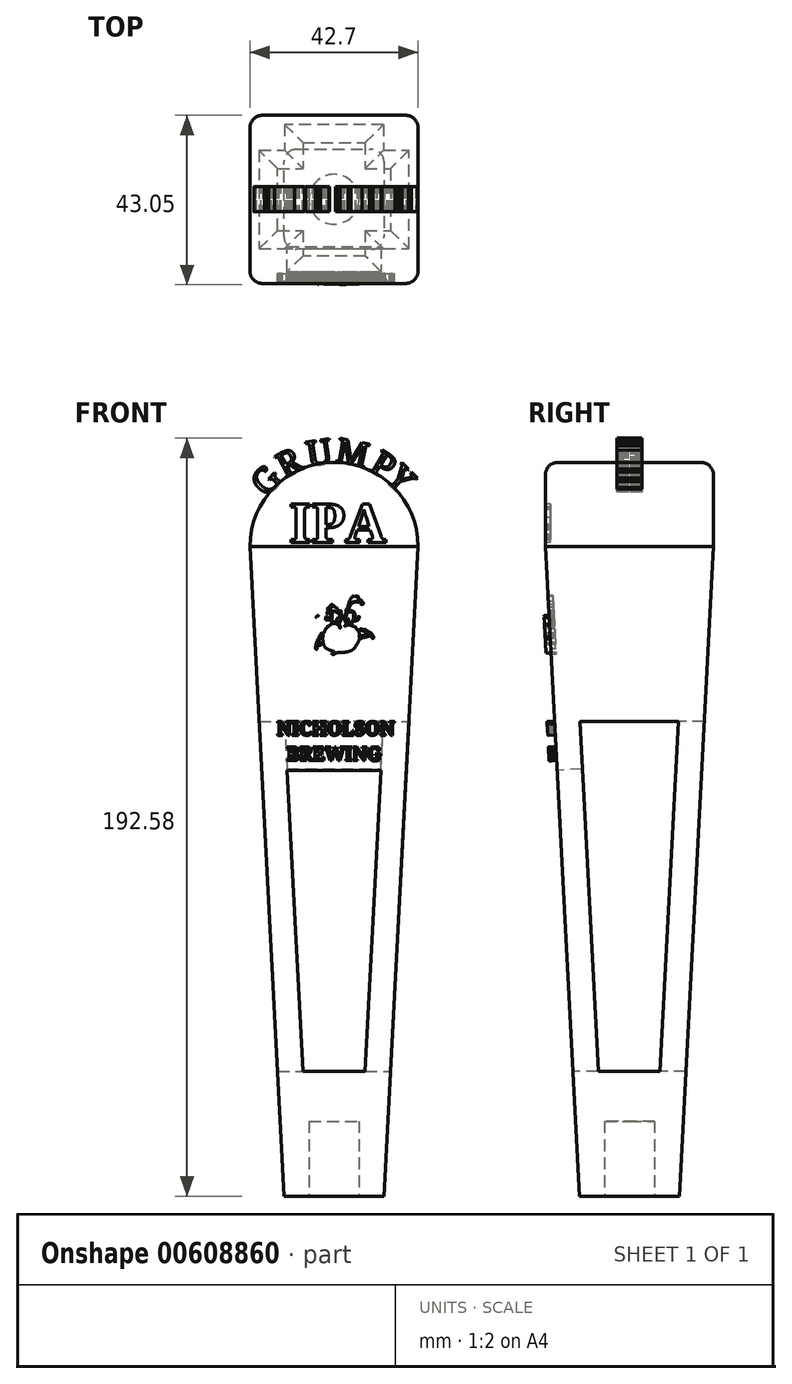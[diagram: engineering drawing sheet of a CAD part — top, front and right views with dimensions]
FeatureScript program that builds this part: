
annotation { "Feature Type Name" : "Feature", "Feature Type Description" : "" }
export const myFeature = defineFeature(function(context is Context, id is Id, definition is map)
    precondition{}
    {
        {
            var Q0;
            Q0=qCreatedBy(makeId("Top.planeOp"),FACE);
            var sketch = newSketch(context, id + "F0", { "sketchPlane" : qUnion([Q0])});
            skLineSegment(sketch, "E0.bottom", {"start": v(12.7, -12.7) * mm, "end": v(-12.7, -12.7) * mm});
            skLineSegment(sketch, "E0.top", {"start": v(12.7, 12.7) * mm, "end": v(-12.7, 12.7) * mm});
            skLineSegment(sketch, "E0.left", {"start": v(12.7, -12.7) * mm, "end": v(12.7, 12.7) * mm});
            skLineSegment(sketch, "E0.right", {"start": v(-12.7, -12.7) * mm, "end": v(-12.7, 12.7) * mm});
            skPoint(sketch, "E0.middle", {"position": v(0, 0) * mm});
            skSolve(sketch);
        }
        {
            var Q0;
            Q0=makeQuery(id+"F0.imprint","IMPRINT",FACE,{"disambiguationData":[TD([[makeQuery(id+"F0.imprint","IMPRINT",EDGE,{"derivedFrom":sQuery(id+"F0.wireOp",EDGE,"E0.bottom")}),-1.0]])]});
            extrude(context, id + "F1", {"entities" : qUnion([Q0]), "depth" : 165.1 * mm, "offsetDistance" : 25.4 * mm, "hasDraft" : true, "draftAngle" : 3 * degree});
        }
        {
            var Q0;
            Q0=qCreatedBy(makeId("Front.planeOp"),FACE);
            var sketch = newSketch(context, id + "F2", { "sketchPlane" : qUnion([Q0])});
            skArc(sketch, "E1", {"start": v(21.35, 165.1) * mm, "mid": v(0, 186.45) * mm, "end": v(-21.35, 165.1) * mm});
            skLineSegment(sketch, "E2", {"start": v(0, 165.1) * mm, "end": v(-21.35, 165.1) * mm});
            skLineSegment(sketch, "E3", {"start": v(-21.35, 165.1) * mm, "end": v(21.35, 165.1) * mm});
            skSolve(sketch);
        }
        {
            var Q0;
            Q0=makeQuery(id+"F1.opExtrude","SWEPT_FACE",FACE,{"disambiguationData":[OSD([sQuery(id+"F0.wireOp",EDGE,"E0.bottom")])]});
            var sketch = newSketch(context, id + "F3", { "sketchPlane" : qUnion([Q0])});
            skFitSpline(sketch, "E4", {"points": [v(-3.93, 148.41) * mm, v(-6, 146.06) * mm, v(-7.77, 144.13) * mm, v(-9.42, 142.29) * mm, v(-9.9, 141.3) * mm, v(-10.32, 140.28) * mm, v(-10.2, 139.42) * mm, v(-10.01, 139.18) * mm, v(-9.58, 140.32) * mm, v(-9.19, 140.67) * mm, v(-9.5, 139.54) * mm, v(-9.58, 138.12) * mm, v(-8.52, 135.3) * mm, v(-7.62, 134.55) * mm, v(-7.5, 135.65) * mm, v(-7.26, 135.68) * mm, v(-7.1, 134.94) * mm, v(-7.19, 133.52) * mm, v(-6.24, 131.8) * mm, v(-4.71, 129.75) * mm, v(-4, 129.4) * mm, v(-4.09, 130.18) * mm, v(-4.09, 131.05) * mm, v(-3.81, 131.24) * mm, v(-3.7, 129.48) * mm, v(-2.9, 128.02) * mm, v(-0.9, 126.3) * mm, v(-0.67, 126.92) * mm, v(0.94, 129.4) * mm, v(3.88, 130.9) * mm, v(6.4, 131.95) * mm, v(7.14, 132.7) * mm, v(7.72, 134.3) * mm, v(8.04, 134.3) * mm, v(8, 133.56) * mm, v(7.69, 132.82) * mm, v(9.3, 133.84) * mm, v(10, 135.02) * mm, v(10.27, 134.9) * mm, v(10.08, 134.03) * mm, v(11.1, 135.37) * mm, v(11.9, 136.77) * mm, v(12.52, 139.46) * mm, v(12.12, 141.58) * mm, v(12.47, 142.22) * mm, v(11.73, 144.3) * mm, v(10.14, 145.79) * mm, v(8.81, 147.12) * mm, v(8.9, 146.18) * mm, v(9.8, 145.34) * mm, v(11.23, 143.21) * mm, v(11.38, 141.78) * mm, v(10.2, 140.59) * mm, v(8.27, 140.14) * mm, v(6.59, 140) * mm, v(5.8, 139.7) * mm, v(6.49, 140.39) * mm, v(5.84, 140.2) * mm, v(4.95, 138.95) * mm, v(3.52, 137.72) * mm, v(1.54, 136.97) * mm, v(-0.63, 137.37) * mm, v(-1.52, 137.96) * mm, v(-2.07, 138.8) * mm, v(-2.16, 139.6) * mm, v(-2.36, 138.8) * mm, v(-3.45, 138.66) * mm, v(-4.34, 138.7) * mm, v(-5.82, 139.35) * mm, v(-6.67, 140.56) * mm, v(-6.75, 142.27) * mm, v(-6.1, 143.76) * mm, v(-5.13, 145.13) * mm, v(-4.32, 146.04) * mm, v(-3.35, 146.65) * mm, v(-3.64, 146.83) * mm, v(-3.84, 146.83) * mm, v(-3.93, 148.41) * mm]});
            skFitSpline(sketch, "E5", {"points": [v(-3.93, 148.41) * mm, v(-3.27, 149.51) * mm, v(-2.97, 151.48) * mm, v(-2.12, 153.44) * mm, v(-0.83, 155.33) * mm, v(1.17, 156.56) * mm, v(3.21, 156.93) * mm, v(5.58, 155.85) * mm, v(7.25, 154.11) * mm, v(8.1, 152.3) * mm, v(8.58, 148.07) * mm, v(9.33, 147.12) * mm, v(9.72, 147.12) * mm, v(9.74, 148) * mm, v(9.69, 149.97) * mm, v(9.35, 152.98) * mm, v(8.03, 155.62) * mm, v(6.08, 157.5) * mm, v(3.87, 158.7) * mm, v(1.8, 158.96) * mm, v(0, 158.5) * mm, v(-2.07, 156.81) * mm, v(-2.76, 155.16) * mm, v(-3.62, 153.34) * mm, v(-3.65, 154.07) * mm, v(-3.12, 155.3) * mm, v(-2.6, 156.78) * mm, v(-1.64, 157.9) * mm, v(-2.9, 157.37) * mm, v(-4.3, 155.92) * mm, v(-4.94, 154.73) * mm, v(-5.46, 152.82) * mm, v(-5.7, 151.63) * mm, v(-5.96, 151.46) * mm, v(-5.96, 151.96) * mm, v(-5.56, 153.74) * mm, v(-6.16, 152.82) * mm, v(-7.6, 151.76) * mm, v(-9.06, 150.83) * mm, v(-10.94, 149.78) * mm, v(-11.73, 148.92) * mm, v(-12.23, 147.66) * mm, v(-12.26, 146.37) * mm, v(-11.8, 145.41) * mm, v(-10.74, 144.72) * mm, v(-9.62, 144.13) * mm, v(-8.53, 144) * mm, v(-7.77, 144.13) * mm, v(-6, 146.06) * mm, v(-6, 146.9) * mm, v(-6, 147.81) * mm, v(-5.51, 147.85) * mm, v(-5.5, 147.12) * mm, v(-5.34, 146.98) * mm, v(-5.24, 147.12) * mm, v(-4.72, 147.8) * mm, v(-4.12, 148.41) * mm, v(-3.93, 148.41) * mm]});
            skFitSpline(sketch, "E6", {"points": [v(9.26, 143.2) * mm, v(9.68, 142.71) * mm, v(9.84, 142.49) * mm, v(10.1, 142.68) * mm, v(10.17, 142.96) * mm, v(9.79, 143.38) * mm, v(9.47, 143.89) * mm, v(8.6, 144.45) * mm, v(7.83, 144.85) * mm, v(7.03, 144.92) * mm, v(6.6, 144.97) * mm, v(6.57, 144.74) * mm, v(7.05, 144.59) * mm, v(8.06, 144.13) * mm, v(8.81, 143.76) * mm, v(8.23, 143.66) * mm, v(7.36, 143.33) * mm, v(6.63, 143.12) * mm, v(6.43, 143.05) * mm, v(6.42, 143.87) * mm, v(6.03, 144.7) * mm, v(5.37, 145.48) * mm, v(4.53, 145.88) * mm, v(4.04, 146.06) * mm, v(3.36, 146.06) * mm, v(2.78, 145.8) * mm, v(2.7, 145.9) * mm, v(3, 146.06) * mm, v(3.15, 146.34) * mm, v(2.85, 146.9) * mm, v(2.73, 147.39) * mm, v(2.7, 147.74) * mm, v(2.33, 147.9) * mm, v(1.9, 147.93) * mm, v(1.82, 147.7) * mm, v(1.84, 147.28) * mm, v(1.68, 147.12) * mm, v(1.43, 146.56) * mm, v(1.43, 146.06) * mm, v(1.63, 145.62) * mm, v(1.63, 145.32) * mm, v(1.47, 145.27) * mm, v(1.36, 145.67) * mm, v(0.98, 146.06) * mm, v(0.5, 146.4) * mm, v(-0.33, 146.39) * mm, v(-1.01, 146.06) * mm, v(-1.92, 145.27) * mm, v(-2.31, 144.6) * mm, v(-2.5, 144.13) * mm, v(-3.04, 143.99) * mm, v(-3.57, 143.42) * mm, v(-4.15, 142.16) * mm, v(-4.6, 140.89) * mm, v(-4.72, 140.12) * mm, v(-4.66, 139.86) * mm, v(-4.31, 139.86) * mm, v(-4.3, 140.34) * mm, v(-4.17, 140.65) * mm, v(-3.55, 140.85) * mm, v(-2.7, 141.16) * mm, v(-2.43, 140.57) * mm, v(-1.88, 140.06) * mm, v(-0.98, 139.6) * mm, v(0, 139.27) * mm, v(0, 139.02) * mm, v(-0.4, 138.86) * mm, v(-0.5, 138.57) * mm, v(0, 138.49) * mm, v(0.36, 138.88) * mm, v(0.79, 139) * mm, v(1.61, 139.02) * mm, v(2.54, 139.08) * mm, v(3.34, 139.22) * mm, v(4.54, 139.67) * mm, v(5.4, 140.36) * mm, v(5.89, 141.28) * mm, v(6.26, 141.79) * mm, v(6.36, 142.18) * mm, v(6.48, 142.44) * mm, v(7.83, 142.85) * mm, v(8.81, 143.14) * mm, v(9.26, 143.2) * mm]});
            skFitSpline(sketch, "E7", {"points": [v(-2.9, 143.68) * mm, v(-3.3, 143.15) * mm, v(-3.66, 142.3) * mm, v(-3.93, 141.14) * mm, v(-3.58, 141.3) * mm, v(-2.77, 141.57) * mm, v(-2.77, 141.82) * mm, v(-2.87, 142.47) * mm, v(-2.9, 143.68) * mm]});
            skFitSpline(sketch, "E8", {"points": [v(4.12, 146.35) * mm, v(3.75, 146.31) * mm, v(3.45, 146.42) * mm, v(3.5, 146.56) * mm, v(3.71, 146.98) * mm, v(3.68, 147.44) * mm, v(3.55, 147.7) * mm, v(3.08, 147.7) * mm, v(2.93, 147.93) * mm, v(3.16, 148.41) * mm, v(3.3, 148.96) * mm, v(3.82, 149.22) * mm, v(4.53, 149.28) * mm, v(4.88, 148.93) * mm, v(4.97, 148.41) * mm, v(4.9, 147.7) * mm, v(4.73, 147.12) * mm, v(4.12, 146.35) * mm]});
            skFitSpline(sketch, "E9", {"points": [v(0.95, 146.85) * mm, v(0.73, 147.12) * mm, v(0.75, 147.54) * mm, v(1.08, 147.9) * mm, v(1.6, 148.1) * mm, v(1.43, 148.6) * mm, v(0.82, 149.11) * mm, v(0.42, 149.4) * mm, v(0, 149.52) * mm, v(-0.36, 149.28) * mm, v(-0.47, 148.74) * mm, v(-0.53, 148.1) * mm, v(-0.55, 147.54) * mm, v(-0.4, 147.12) * mm, v(0, 146.72) * mm, v(0.48, 146.78) * mm, v(0.95, 146.85) * mm]});
            skFitSpline(sketch, "E10", {"points": [v(3.53, 149.67) * mm, v(3.91, 150.38) * mm, v(4.1, 151.02) * mm, v(4.46, 151.46) * mm, v(5.1, 151.83) * mm, v(5.73, 151.88) * mm, v(6.25, 151.88) * mm, v(6.6, 151.7) * mm, v(6.8, 151.32) * mm, v(7.16, 151.14) * mm, v(7.44, 151.46) * mm, v(7.18, 152) * mm, v(6.73, 152.4) * mm, v(6.47, 152.58) * mm, v(6.1, 152.67) * mm, v(6.09, 152.82) * mm, v(6.2, 153.1) * mm, v(6.12, 153.29) * mm, v(5.51, 153.35) * mm, v(5.22, 153.15) * mm, v(5.05, 153.27) * mm, v(4.85, 153.42) * mm, v(4.62, 153.24) * mm, v(4.01, 152.15) * mm, v(3.7, 151.3) * mm, v(3.48, 150.56) * mm, v(3.37, 150.15) * mm, v(3.05, 149.88) * mm, v(3.04, 149.24) * mm, v(2.84, 148.6) * mm, v(2.6, 148.23) * mm, v(2.1, 148.3) * mm, v(1.9, 148.73) * mm, v(1.82, 149.24) * mm, v(1.82, 149.55) * mm, v(1.43, 149.52) * mm, v(1.19, 149.47) * mm, v(0.98, 149.85) * mm, v(0.65, 150.35) * mm, v(0.23, 150.64) * mm, v(-0.21, 151.06) * mm, v(-0.67, 151.19) * mm, v(-0.87, 151.06) * mm, v(-0.7, 150.77) * mm, v(-0.46, 150.53) * mm, v(-0.8, 150.46) * mm, v(-1.25, 150.58) * mm, v(-1.55, 150.26) * mm, v(-1.78, 150.05) * mm, v(-1.28, 149.93) * mm, v(-1.1, 149.9) * mm, v(-1.73, 149.3) * mm, v(-1.8, 148.94) * mm, v(-1.65, 148.84) * mm, v(-1.33, 149.12) * mm, v(-0.92, 149.52) * mm, v(-0.7, 149.57) * mm, v(-0.6, 149.29) * mm, v(-0.84, 148.9) * mm, v(-0.87, 148.41) * mm, v(-0.79, 147.93) * mm, v(-0.77, 147.7) * mm, v(-0.8, 147.52) * mm, v(-0.96, 147.4) * mm, v(-1.27, 147.6) * mm, v(-1.62, 147.9) * mm, v(-1.75, 148.02) * mm, v(-1.95, 148.12) * mm, v(-2.1, 147.93) * mm, v(-2.1, 147.5) * mm, v(-2.1, 147.32) * mm, v(-1.47, 147.26) * mm, v(-0.92, 147.12) * mm, v(-0.51, 146.8) * mm, v(-0.33, 146.39) * mm, v(-0.18, 146.42) * mm, v(0.2, 146.45) * mm, v(0.5, 146.4) * mm, v(0.98, 146.06) * mm, v(1.36, 145.67) * mm, v(1.47, 145.27) * mm, v(1.63, 145.32) * mm, v(1.63, 145.62) * mm, v(1.43, 146.06) * mm, v(1.43, 146.56) * mm, v(1.68, 147.12) * mm, v(1.84, 147.28) * mm, v(1.82, 147.7) * mm, v(1.9, 147.93) * mm, v(2.33, 147.9) * mm, v(2.7, 147.74) * mm, v(2.73, 147.39) * mm, v(2.85, 146.9) * mm, v(3.15, 146.34) * mm, v(3, 146.06) * mm, v(2.7, 145.9) * mm, v(2.78, 145.8) * mm, v(3.36, 146.06) * mm, v(4.04, 146.06) * mm, v(4.3, 145.97) * mm, v(4.35, 146.06) * mm, v(4.35, 146.34) * mm, v(4.62, 146.56) * mm, v(4.9, 146.84) * mm, v(5.37, 147.03) * mm, v(5.8, 147.12) * mm, v(6.18, 147.33) * mm, v(6.27, 147.54) * mm, v(6.34, 147.7) * mm, v(6.53, 147.93) * mm, v(6.36, 148.13) * mm, v(6.02, 148.04) * mm, v(5.79, 147.7) * mm, v(5.67, 147.7) * mm, v(5.43, 147.42) * mm, v(5.1, 147.12) * mm, v(5.1, 147.4) * mm, v(5.26, 148.3) * mm, v(5.3, 148.7) * mm, v(5.23, 149.08) * mm, v(5, 149.42) * mm, v(4.42, 149.64) * mm, v(3.96, 149.58) * mm, v(3.6, 149.47) * mm, v(3.52, 149.53) * mm, v(3.53, 149.67) * mm]});
            skLineSegment(sketch, "E11", {"start": v(-2.9, 143.68) * mm, "end": v(-3.04, 143.99) * mm});
            skLineSegment(sketch, "E12", {"start": v(-2.9, 143.68) * mm, "end": v(-2.5, 144.13) * mm});
            skLineSegment(sketch, "E13", {"start": v(-2.77, 141.57) * mm, "end": v(-2.7, 141.16) * mm});
            skLineSegment(sketch, "E14", {"start": v(0, 139.02) * mm, "end": v(0.36, 138.88) * mm});
            skLineSegment(sketch, "E15", {"start": v(6.48, 142.44) * mm, "end": v(6.43, 143.05) * mm});
            skSolve(sketch);
        }
        {
            var Q0;
            {var subQ0=sQuery(id+"F3.wireOp",EDGE,"E11");Q0=makeQuery(id+"F3.imprint","IMPRINT",FACE,{"disambiguationData":[TD([[makeQuery(id+"F3.imprint","IMPRINT",EDGE,{"derivedFrom":subQ0}),1.0]])]});}
            var Q1;
            {var subQ0=sQuery(id+"F3.wireOp",EDGE,"E14");Q1=makeQuery(id+"F3.imprint","IMPRINT",FACE,{"disambiguationData":[TD([[makeQuery(id+"F3.imprint","IMPRINT",EDGE,{"derivedFrom":subQ0}),-1.0]])]});}
            var Q2;
            {var subQ0=sQuery(id+"F3.wireOp",EDGE,"E15");Q2=makeQuery(id+"F3.imprint","IMPRINT",FACE,{"disambiguationData":[TD([[makeQuery(id+"F3.imprint","IMPRINT",EDGE,{"derivedFrom":subQ0}),-1.0]])]});}
            var Q3;
            Q3=makeQuery(id+"F3.imprint","IMPRINT",FACE,{"disambiguationData":[TD([[makeQuery(id+"F3.imprint","IMPRINT",EDGE,{"derivedFrom":sQuery(id+"F3.wireOp",EDGE,"E8")}),1.0]])]});
            extrude(context, id + "F4", {"entities" : qUnion([Q0, Q1, Q2, Q3]), "operationType" : NewBodyOperationType.REMOVE, "oppositeDirection" : true, "depth" : 1.27 * mm, "offsetDistance" : 25.4 * mm});
        }
        {
            var Q0;
            {var subQ0=sQuery(id+"F3.wireOp",EDGE,"E5");var subQ1=sQuery(id+"F3.wireOp",EDGE,"E4");var subQ7=makeQuery(id+"F3.imprint","INTERSECT",VERTEX,{"disambiguationData":[OD(2.0)],"derivedFrom":[subQ1,subQ0]});Q0=makeQuery(id+"F3.imprint","IMPRINT",FACE,{"disambiguationData":[TD([[makeQuery(id+"F3.imprint","IMPRINT",EDGE,{"disambiguationData":[TD([[subQ7,1.0]])],"derivedFrom":subQ1}),-1.0]])]});}
            extrude(context, id + "F5", {"entities" : qUnion([Q0]), "operationType" : NewBodyOperationType.REMOVE, "oppositeDirection" : true, "depth" : 1.27 * mm, "offsetDistance" : 25.4 * mm});
        }
        {
            var Q0;
            {var subQ0=sQuery(id+"F3.wireOp",EDGE,"E5");var subQ1=sQuery(id+"F3.wireOp",EDGE,"E4");var subQ8=makeQuery(id+"F3.imprint","INTERSECT",VERTEX,{"disambiguationData":[OD(0.0)],"derivedFrom":[subQ1,subQ0]});Q0=makeQuery(id+"F3.imprint","IMPRINT",FACE,{"disambiguationData":[TD([[makeQuery(id+"F3.imprint","IMPRINT",EDGE,{"disambiguationData":[TD([[subQ8,1.0]])],"derivedFrom":subQ1}),1.0]])]});}
            var Q1;
            {var subQ9=sQuery(id+"F3.wireOp",EDGE,"E12");Q1=makeQuery(id+"F3.imprint","IMPRINT",FACE,{"disambiguationData":[TD([[makeQuery(id+"F3.imprint","IMPRINT",EDGE,{"derivedFrom":subQ9}),-1.0]])]});}
            extrude(context, id + "F6", {"entities" : qUnion([Q0, Q1]), "operationType" : NewBodyOperationType.ADD, "depth" : 1.27 * mm, "offsetDistance" : 25.4 * mm});
        }
        {
            var Q0;
            Q0=makeQuery(id+"F1.opExtrude","CAP_FACE",FACE,{"disambiguationData":[OSD([sQuery(id+"F0.wireOp",EDGE,"E0.bottom"),sQuery(id+"F0.wireOp",EDGE,"E0.top"),sQuery(id+"F0.wireOp",EDGE,"E0.left"),sQuery(id+"F0.wireOp",EDGE,"E0.right")])],"isStart":false});
            var sketch = newSketch(context, id + "F7", { "sketchPlane" : qUnion([Q0])});
            skLineSegment(sketch, "E16.bottom", {"start": v(-21.35, 21.35) * mm, "end": v(21.35, 21.35) * mm});
            skLineSegment(sketch, "E16.top", {"start": v(-21.35, -21.35) * mm, "end": v(21.35, -21.35) * mm});
            skLineSegment(sketch, "E16.left", {"start": v(-21.35, 21.35) * mm, "end": v(-21.35, -21.35) * mm});
            skLineSegment(sketch, "E16.right", {"start": v(21.35, 21.35) * mm, "end": v(21.35, -21.35) * mm});
            skSolve(sketch);
        }
        {
            var Q0;
            {var subQ0=sQuery(id+"F2.wireOp",EDGE,"E1");Q0=makeQuery(id+"F2.imprint","IMPRINT",FACE,{"disambiguationData":[TD([[makeQuery(id+"F2.imprint","IMPRINT",EDGE,{"derivedFrom":subQ0}),1.0]])]});}
            extrude(context, id + "F8", {"entities" : qUnion([Q0]), "operationType" : NewBodyOperationType.ADD, "depth" : 21.35 * mm, "offsetDistance" : 25.4 * mm, "hasSecondDirection" : true, "secondDirectionOppositeDirection" : true, "secondDirectionDepth" : 21.35 * mm});
        }
        {
            var Q0;
            Q0=qCreatedBy(makeId("Front.planeOp"),FACE);
            var sketch = newSketch(context, id + "F9", { "sketchPlane" : qUnion([Q0])});
            skLineSegment(sketch, "E17", {"start": v(0, 0) * mm, "end": v(0, 31.75) * mm, "construction": true});
            skLineSegment(sketch, "E18", {"start": v(0, 31.75) * mm, "end": v(-7.91, 31.75) * mm});
            skLineSegment(sketch, "E19", {"start": v(-7.91, 31.75) * mm, "end": v(-12.57, 120.65) * mm});
            skLineSegment(sketch, "E20", {"start": v(-12.57, 120.65) * mm, "end": v(12.57, 120.65) * mm});
            skLineSegment(sketch, "E21", {"start": v(12.57, 120.65) * mm, "end": v(7.91, 31.75) * mm});
            skLineSegment(sketch, "E22", {"start": v(7.91, 31.75) * mm, "end": v(0, 31.75) * mm});
            skLineSegment(sketch, "E23", {"start": v(0, 31.75) * mm, "end": v(0, 31.75) * mm});
            skSolve(sketch);
        }
        {
            var Q0;
            Q0 = qSketchRegion(id + "F9", true);
            extrude(context, id + "F10", {"entities" : qUnion([Q0]), "operationType" : NewBodyOperationType.REMOVE, "oppositeDirection" : true, "depth" : 25.4 * mm, "offsetDistance" : 25.4 * mm, "hasSecondDirection" : true, "secondDirectionOppositeDirection" : false, "secondDirectionDepth" : 25.4 * mm});
        }
        {
            var Q0;
            Q0=qCreatedBy(makeId("Right.planeOp"),FACE);
            var sketch = newSketch(context, id + "F11", { "sketchPlane" : qUnion([Q0])});
            skLineSegment(sketch, "E24", {"start": v(0, 0) * mm, "end": v(0, 31.75) * mm, "construction": true});
            skLineSegment(sketch, "E25", {"start": v(0, 31.75) * mm, "end": v(-7.91, 31.75) * mm});
            skLineSegment(sketch, "E26", {"start": v(-7.91, 31.75) * mm, "end": v(-12.57, 120.65) * mm});
            skLineSegment(sketch, "E27", {"start": v(-12.57, 120.65) * mm, "end": v(12.44, 120.65) * mm});
            skLineSegment(sketch, "E28", {"start": v(12.44, 120.65) * mm, "end": v(7.78, 31.75) * mm});
            skLineSegment(sketch, "E29", {"start": v(7.78, 31.75) * mm, "end": v(0, 31.75) * mm});
            skSolve(sketch);
        }
        {
            var Q0;
            Q0 = qSketchRegion(id + "F11", true);
            extrude(context, id + "F12", {"entities" : qUnion([Q0]), "operationType" : NewBodyOperationType.REMOVE, "oppositeDirection" : true, "depth" : 25.4 * mm, "offsetDistance" : 25.4 * mm, "hasSecondDirection" : true, "secondDirectionOppositeDirection" : false, "secondDirectionDepth" : 25.4 * mm});
        }
        {
            var Q0;
            Q0=makeQuery(id+"F8.opExtrude","CAP_FACE",FACE,{"disambiguationData":[OSD([sQuery(id+"F2.wireOp",EDGE,"E1"),sQuery(id+"F2.wireOp",EDGE,"E3")])],"isStart":false});
            var sketch = newSketch(context, id + "F13", { "sketchPlane" : qUnion([Q0])});
            skText(sketch, "E30", { "text": "IPA", "fontName": "NotoSerif-Bold.ttf"});
            const initialGuessF13  = {"E30": [-0.01126, 0.1661, 1, 0, 0.00982]};
            skSetInitialGuess(sketch, initialGuessF13);
            skSolve(sketch);
        }
        {
            var Q0;
            Q0 = qSketchRegion(id + "F13", true);
            extrude(context, id + "F14", {"entities" : qUnion([Q0]), "operationType" : NewBodyOperationType.REMOVE, "oppositeDirection" : true, "depth" : 1.27 * mm, "offsetDistance" : 25.4 * mm});
        }
        {
            var Q0;
            Q0=qCreatedBy(makeId("Front.planeOp"),FACE);
            var sketch = newSketch(context, id + "F15", { "sketchPlane" : qUnion([Q0])});
            skText(sketch, "E31", { "text": "G", "fontName": "NotoSerif-Regular.ttf"});
            skLineSegment(sketch, "E32", {"start": v(0, 165.1) * mm, "end": v(-14.95, 179.79) * mm, "construction": true});
            skLineSegment(sketch, "E33", {"start": v(0, 165.1) * mm, "end": v(-9.68, 183.69) * mm, "construction": true});
            skText(sketch, "E34", { "text": "R", "fontName": "NotoSerif-Regular.ttf"});
            skText(sketch, "E35", { "text": "U", "fontName": "NotoSerif-Regular.ttf"});
            skLineSegment(sketch, "E36", {"start": v(0, 165.1) * mm, "end": v(-3.1, 185.82) * mm, "construction": true});
            skText(sketch, "E37", { "text": "M", "fontName": "NotoSerif-Regular.ttf"});
            skLineSegment(sketch, "E38", {"start": v(0, 165.1) * mm, "end": v(4.18, 185.63) * mm, "construction": true});
            skText(sketch, "E39", { "text": "P", "fontName": "NotoSerif-Regular.ttf"});
            skLineSegment(sketch, "E40", {"start": v(0, 165.1) * mm, "end": v(10.95, 182.97) * mm, "construction": true});
            skText(sketch, "E41", { "text": "Y", "fontName": "NotoSerif-Regular.ttf"});
            skLineSegment(sketch, "E42", {"start": v(0, 165.1) * mm, "end": v(14.95, 179.79) * mm, "construction": true});
            const initialGuessF15  = {"E31": [-0.0173, 0.1774, 0.7009, 0.71325, 0.00635], "E34": [-0.01252, 0.1822, 0.88701, 0.46175, 0.00635], "E35": [-0.00644, 0.18532, 0.98902, 0.1478, 0.00635], "E37": [0, 0.18648, 0.97992, -0.19937, 0.00635], "E39": [0.00858, 0.18442, 0.85264, -0.5225, 0.00635], "E41": [0.01279, 0.18198, 0.7009, -0.71325, 0.00635]};
            skSetInitialGuess(sketch, initialGuessF15);
            skSolve(sketch);
        }
        {
            var Q0;
            Q0 = qSketchRegion(id + "F15", true);
            extrude(context, id + "F16", {"entities" : qUnion([Q0]), "depth" : 3.17 * mm, "offsetDistance" : 25.4 * mm, "hasSecondDirection" : true, "secondDirectionOppositeDirection" : true, "secondDirectionDepth" : 3.17 * mm});
        }
        {
            var Q0;
            {var subQ0=sQuery(id+"F3.wireOp",EDGE,"E15");var subQ1=sQuery(id+"F3.wireOp",EDGE,"E6");var subQ2=makeQuery(id+"F3.imprint","INTERSECT",VERTEX,{"disambiguationData":[OD(0.0)],"derivedFrom":[subQ1,subQ0]});var subQ3=sQuery(id+"F3.wireOp",EDGE,"E10");var subQ4=makeQuery(id+"F3.imprint","INTERSECT",VERTEX,{"disambiguationData":[OD(0.0)],"derivedFrom":[subQ1,subQ3]});var subQ5=sQuery(id+"F3.wireOp",EDGE,"E5");var subQ6=sQuery(id+"F3.wireOp",EDGE,"E4");var subQ7=makeQuery(id+"F3.imprint","INTERSECT",VERTEX,{"disambiguationData":[OD(2.0)],"derivedFrom":[subQ6,subQ5]});var subQ8=makeQuery(id+"F3.imprint","INTERSECT",VERTEX,{"disambiguationData":[OD(3.0)],"derivedFrom":[subQ6,subQ5]});var subQ9=sQuery(id+"F0.wireOp",EDGE,"E0.right");var subQ10=makeQuery(id+"F1.opExtrude","SWEPT_FACE",FACE,{"disambiguationData":[OSD([subQ9])]});var subQ11=makeQuery(id+"F3.imprint","INTERSECT",VERTEX,{"disambiguationData":[OD(6.0)],"derivedFrom":[subQ6,subQ5]});var subQ13=sQuery(id+"F0.wireOp",EDGE,"E0.left");var subQ14=sQuery(id+"F0.wireOp",EDGE,"E0.top");var subQ15=sQuery(id+"F0.wireOp",EDGE,"E0.bottom");var subQ16=makeQuery(id+"F1.opExtrude","CAP_FACE",FACE,{"disambiguationData":[OSD([subQ15,subQ14,subQ13,subQ9])],"isStart":false});var subQ17=sQuery(id+"F3.wireOp",EDGE,"E14");var subQ18=makeQuery(id+"F3.imprint","INTERSECT",VERTEX,{"disambiguationData":[OD(0.0)],"derivedFrom":[subQ1,subQ17]});var subQ19=makeQuery(id+"F3.imprint","INTERSECT",VERTEX,{"disambiguationData":[OD(1.0)],"derivedFrom":[subQ1,subQ17]});var subQ20=makeQuery(id+"F4.opExtrude","SWEPT_FACE",FACE,{"disambiguationData":[OSD([subQ1]),TDD([makeQuery(id+"F3.imprint","IMPRINT",EDGE,{"disambiguationData":[TD([[subQ18,-1.0]])],"derivedFrom":subQ1})])]});var subQ21=sQuery(id+"F3.wireOp",EDGE,"E13");var subQ22=makeQuery(id+"F4.opExtrude","SWEPT_FACE",FACE,{"disambiguationData":[OSD([subQ0])]});var subQ23=makeQuery(id+"F4.opExtrude","SWEPT_FACE",FACE,{"disambiguationData":[OSD([subQ17])]});var subQ24=makeQuery(id+"F4.opExtrude","SWEPT_FACE",FACE,{"disambiguationData":[OSD([subQ21])]});var subQ25=sQuery(id+"F3.wireOp",EDGE,"E11");var subQ26=makeQuery(id+"F4.opExtrude","SWEPT_FACE",FACE,{"disambiguationData":[OSD([subQ25])]});var subQ29=makeQuery(id+"F4.opExtrude","SWEPT_FACE",FACE,{"disambiguationData":[OSD([subQ3]),TDD([makeQuery(id+"F3.imprint","IMPRINT",EDGE,{"disambiguationData":[TD([[subQ4,1.0]])],"derivedFrom":subQ3}),makeQuery(id+"F3.imprint","IMPRINT",EDGE,{"disambiguationData":[TD([[subQ4,-1.0]])],"derivedFrom":subQ3})])]});var subQ30=makeQuery(id+"F1.opExtrude","SWEPT_FACE",FACE,{"disambiguationData":[OSD([subQ13])]});var subQ31=makeQuery(id+"F1.opExtrude","CAP_FACE",FACE,{"disambiguationData":[OSD([subQ15,subQ14,subQ13,subQ9])],"isStart":true});var subQ32=makeQuery(id+"F3.imprint","INTERSECT",VERTEX,{"derivedFrom":[subQ1,subQ21]});var subQ33=makeQuery(id+"F4.opExtrude","SWEPT_FACE",FACE,{"disambiguationData":[OSD([subQ1]),TDD([makeQuery(id+"F3.imprint","IMPRINT",EDGE,{"disambiguationData":[TD([[makeQuery(id+"F3.imprint","INTERSECT",VERTEX,{"derivedFrom":[subQ1,subQ25]}),-1.0]])],"derivedFrom":subQ1})])]});var subQ34=sQuery(id+"F3.wireOp",EDGE,"E12");var subQ35=makeQuery(id+"F1.opExtrude","SWEPT_FACE",FACE,{"disambiguationData":[OSD([subQ15])]});var subQ36=makeQuery(id+"F3.imprint","INTERSECT",VERTEX,{"disambiguationData":[OD(7.0)],"derivedFrom":[subQ1,subQ3]});var subQ37=makeQuery(id+"F4.opExtrude","SWEPT_FACE",FACE,{"disambiguationData":[OSD([subQ1]),TDD([makeQuery(id+"F3.imprint","IMPRINT",EDGE,{"disambiguationData":[TD([[subQ36,-1.0]])],"derivedFrom":subQ1})])]});var subQ39=makeQuery(id+"F4.opExtrude","SWEPT_FACE",FACE,{"disambiguationData":[OSD([subQ1]),TDD([makeQuery(id+"F3.imprint","IMPRINT",EDGE,{"disambiguationData":[TD([[subQ2,1.0]])],"derivedFrom":subQ1})])]});var subQ40=sQuery(id+"F3.wireOp",EDGE,"E7");var subQ41=makeQuery(id+"F4.opExtrude","SWEPT_FACE",FACE,{"disambiguationData":[OSD([subQ40])]});Q0=makeQuery(id+"F6.boolean.opBoolean","SPLIT",FACE,{"disambiguationData":[TD([subQ35,subQ31,subQ16,subQ30,subQ10,makeQuery(id+"F4.boolean.opBoolean","COPY",FACE,{"derivedFrom":subQ37}),makeQuery(id+"F4.boolean.opBoolean","COPY",FACE,{"derivedFrom":subQ33}),makeQuery(id+"F4.boolean.opBoolean","COPY",FACE,{"derivedFrom":subQ20}),makeQuery(id+"F4.boolean.opBoolean","COPY",FACE,{"derivedFrom":subQ39}),makeQuery(id+"F4.boolean.opBoolean","COPY",FACE,{"derivedFrom":subQ41}),makeQuery(id+"F4.boolean.opBoolean","COPY",FACE,{"derivedFrom":subQ29}),makeQuery(id+"F4.boolean.opBoolean","COPY",FACE,{"derivedFrom":subQ26}),makeQuery(id+"F4.boolean.opBoolean","COPY",FACE,{"derivedFrom":subQ24}),makeQuery(id+"F4.boolean.opBoolean","COPY",FACE,{"derivedFrom":subQ23}),makeQuery(id+"F4.boolean.opBoolean","COPY",FACE,{"derivedFrom":subQ22}),makeQuery(id+"F5.boolean.opBoolean","COPY",FACE,{"derivedFrom":makeQuery(id+"F5.opExtrude","SWEPT_FACE",FACE,{"disambiguationData":[OSD([subQ6]),TDD([makeQuery(id+"F3.imprint","IMPRINT",EDGE,{"disambiguationData":[TD([[subQ7,1.0]])],"derivedFrom":subQ6})])]})}),makeQuery(id+"F5.boolean.opBoolean","COPY",FACE,{"derivedFrom":makeQuery(id+"F5.opExtrude","SWEPT_FACE",FACE,{"disambiguationData":[OSD([subQ6]),TDD([makeQuery(id+"F3.imprint","IMPRINT",EDGE,{"disambiguationData":[TD([[subQ11,-1.0]])],"derivedFrom":subQ6})])]})}),makeQuery(id+"F5.boolean.opBoolean","COPY",FACE,{"derivedFrom":makeQuery(id+"F5.opExtrude","SWEPT_FACE",FACE,{"disambiguationData":[OSD([subQ5]),TDD([makeQuery(id+"F3.imprint","IMPRINT",EDGE,{"disambiguationData":[TD([[subQ8,-1.0]])],"derivedFrom":subQ5})])]})}),makeQuery(id+"F6.opExtrude","SWEPT_FACE",FACE,{"disambiguationData":[OSD([subQ6]),TDD([makeQuery(id+"F3.imprint","IMPRINT",EDGE,{"disambiguationData":[TD([[subQ8,1.0]])],"derivedFrom":subQ6})])]}),makeQuery(id+"F6.opExtrude","SWEPT_FACE",FACE,{"disambiguationData":[OSD([subQ5]),TDD([makeQuery(id+"F3.imprint","IMPRINT",EDGE,{"disambiguationData":[TD([[subQ11,1.0]])],"derivedFrom":subQ5})])]}),makeQuery(id+"F6.opExtrude","SWEPT_FACE",FACE,{"disambiguationData":[OSD([subQ5]),TDD([makeQuery(id+"F3.imprint","IMPRINT",EDGE,{"disambiguationData":[TD([[subQ7,-1.0]])],"derivedFrom":subQ5})])]}),makeQuery(id+"F6.opExtrude","SWEPT_FACE",FACE,{"disambiguationData":[OSD([subQ1]),TDD([makeQuery(id+"F3.imprint","IMPRINT",EDGE,{"disambiguationData":[TD([[subQ2,-1.0]])],"derivedFrom":subQ1})])]}),makeQuery(id+"F6.opExtrude","CAP_FACE",FACE,{"disambiguationData":[OSD([subQ1,subQ40,subQ3,subQ34,subQ21,subQ17,subQ0])],"isStart":true}),makeQuery(id+"F6.opExtrude","SWEPT_FACE",FACE,{"disambiguationData":[OSD([subQ1]),TDD([makeQuery(id+"F3.imprint","IMPRINT",EDGE,{"disambiguationData":[TD([[makeQuery(id+"F3.imprint","INTERSECT",VERTEX,{"derivedFrom":[subQ1,subQ34]}),1.0]])],"derivedFrom":subQ1})])]}),makeQuery(id+"F6.opExtrude","SWEPT_FACE",FACE,{"disambiguationData":[OSD([subQ1]),TDD([makeQuery(id+"F3.imprint","IMPRINT",EDGE,{"disambiguationData":[TD([[subQ32,-1.0]])],"derivedFrom":subQ1})])]}),makeQuery(id+"F6.opExtrude","SWEPT_FACE",FACE,{"disambiguationData":[OSD([subQ1]),TDD([makeQuery(id+"F3.imprint","IMPRINT",EDGE,{"disambiguationData":[TD([[subQ19,-1.0]])],"derivedFrom":subQ1})])]}),makeQuery(id+"F6.opExtrude","SWEPT_FACE",FACE,{"disambiguationData":[OSD([subQ40])]}),makeQuery(id+"F6.opExtrude","SWEPT_FACE",FACE,{"disambiguationData":[OSD([subQ3]),TDD([makeQuery(id+"F3.imprint","IMPRINT",EDGE,{"disambiguationData":[TD([[subQ36,1.0]])],"derivedFrom":subQ3})])]}),makeQuery(id+"F6.opExtrude","SWEPT_FACE",FACE,{"disambiguationData":[OSD([subQ34])]}),makeQuery(id+"F6.opExtrude","SWEPT_FACE",FACE,{"disambiguationData":[OSD([subQ21])]}),makeQuery(id+"F6.opExtrude","SWEPT_FACE",FACE,{"disambiguationData":[OSD([subQ17])]}),makeQuery(id+"F6.opExtrude","SWEPT_FACE",FACE,{"disambiguationData":[OSD([subQ0])]})])],"derivedFrom":makeQuery(id+"F4.boolean.opBoolean","SPLIT",FACE,{"disambiguationData":[TD([subQ30])],"derivedFrom":subQ35})});}
            var sketch = newSketch(context, id + "F17", { "sketchPlane" : qUnion([Q0])});
            skLineSegment(sketch, "E43.bottom", {"start": v(-12.57, 121.48) * mm, "end": v(13.38, 121.48) * mm});
            skLineSegment(sketch, "E43.top", {"start": v(-12.57, 109) * mm, "end": v(13.38, 109) * mm});
            skLineSegment(sketch, "E43.left", {"start": v(-12.57, 121.48) * mm, "end": v(-12.57, 109) * mm});
            skLineSegment(sketch, "E43.right", {"start": v(13.38, 121.48) * mm, "end": v(13.38, 109) * mm});
            skSolve(sketch);
        }
        {
            var Q0;
            {var subQ0=sQuery(id+"F3.wireOp",EDGE,"E15");var subQ1=sQuery(id+"F3.wireOp",EDGE,"E6");var subQ2=makeQuery(id+"F3.imprint","INTERSECT",VERTEX,{"disambiguationData":[OD(0.0)],"derivedFrom":[subQ1,subQ0]});var subQ3=sQuery(id+"F3.wireOp",EDGE,"E10");var subQ4=makeQuery(id+"F3.imprint","INTERSECT",VERTEX,{"disambiguationData":[OD(0.0)],"derivedFrom":[subQ1,subQ3]});var subQ5=sQuery(id+"F3.wireOp",EDGE,"E5");var subQ6=sQuery(id+"F3.wireOp",EDGE,"E4");var subQ7=makeQuery(id+"F3.imprint","INTERSECT",VERTEX,{"disambiguationData":[OD(2.0)],"derivedFrom":[subQ6,subQ5]});var subQ8=makeQuery(id+"F3.imprint","INTERSECT",VERTEX,{"disambiguationData":[OD(3.0)],"derivedFrom":[subQ6,subQ5]});var subQ9=sQuery(id+"F0.wireOp",EDGE,"E0.right");var subQ10=makeQuery(id+"F1.opExtrude","SWEPT_FACE",FACE,{"disambiguationData":[OSD([subQ9])]});var subQ11=makeQuery(id+"F3.imprint","INTERSECT",VERTEX,{"disambiguationData":[OD(6.0)],"derivedFrom":[subQ6,subQ5]});var subQ13=sQuery(id+"F0.wireOp",EDGE,"E0.left");var subQ14=sQuery(id+"F0.wireOp",EDGE,"E0.top");var subQ15=sQuery(id+"F0.wireOp",EDGE,"E0.bottom");var subQ16=makeQuery(id+"F1.opExtrude","CAP_FACE",FACE,{"disambiguationData":[OSD([subQ15,subQ14,subQ13,subQ9])],"isStart":false});var subQ17=sQuery(id+"F3.wireOp",EDGE,"E14");var subQ18=makeQuery(id+"F3.imprint","INTERSECT",VERTEX,{"disambiguationData":[OD(0.0)],"derivedFrom":[subQ1,subQ17]});var subQ19=makeQuery(id+"F3.imprint","INTERSECT",VERTEX,{"disambiguationData":[OD(1.0)],"derivedFrom":[subQ1,subQ17]});var subQ20=makeQuery(id+"F4.opExtrude","SWEPT_FACE",FACE,{"disambiguationData":[OSD([subQ1]),TDD([makeQuery(id+"F3.imprint","IMPRINT",EDGE,{"disambiguationData":[TD([[subQ18,-1.0]])],"derivedFrom":subQ1})])]});var subQ21=sQuery(id+"F3.wireOp",EDGE,"E13");var subQ22=makeQuery(id+"F4.opExtrude","SWEPT_FACE",FACE,{"disambiguationData":[OSD([subQ0])]});var subQ23=makeQuery(id+"F4.opExtrude","SWEPT_FACE",FACE,{"disambiguationData":[OSD([subQ17])]});var subQ24=makeQuery(id+"F4.opExtrude","SWEPT_FACE",FACE,{"disambiguationData":[OSD([subQ21])]});var subQ25=sQuery(id+"F3.wireOp",EDGE,"E11");var subQ26=makeQuery(id+"F4.opExtrude","SWEPT_FACE",FACE,{"disambiguationData":[OSD([subQ25])]});var subQ29=makeQuery(id+"F4.opExtrude","SWEPT_FACE",FACE,{"disambiguationData":[OSD([subQ3]),TDD([makeQuery(id+"F3.imprint","IMPRINT",EDGE,{"disambiguationData":[TD([[subQ4,1.0]])],"derivedFrom":subQ3}),makeQuery(id+"F3.imprint","IMPRINT",EDGE,{"disambiguationData":[TD([[subQ4,-1.0]])],"derivedFrom":subQ3})])]});var subQ30=makeQuery(id+"F1.opExtrude","SWEPT_FACE",FACE,{"disambiguationData":[OSD([subQ13])]});var subQ31=makeQuery(id+"F1.opExtrude","CAP_FACE",FACE,{"disambiguationData":[OSD([subQ15,subQ14,subQ13,subQ9])],"isStart":true});var subQ32=makeQuery(id+"F3.imprint","INTERSECT",VERTEX,{"derivedFrom":[subQ1,subQ21]});var subQ33=makeQuery(id+"F4.opExtrude","SWEPT_FACE",FACE,{"disambiguationData":[OSD([subQ1]),TDD([makeQuery(id+"F3.imprint","IMPRINT",EDGE,{"disambiguationData":[TD([[makeQuery(id+"F3.imprint","INTERSECT",VERTEX,{"derivedFrom":[subQ1,subQ25]}),-1.0]])],"derivedFrom":subQ1})])]});var subQ34=sQuery(id+"F3.wireOp",EDGE,"E12");var subQ35=makeQuery(id+"F1.opExtrude","SWEPT_FACE",FACE,{"disambiguationData":[OSD([subQ15])]});var subQ36=makeQuery(id+"F3.imprint","INTERSECT",VERTEX,{"disambiguationData":[OD(7.0)],"derivedFrom":[subQ1,subQ3]});var subQ37=makeQuery(id+"F4.opExtrude","SWEPT_FACE",FACE,{"disambiguationData":[OSD([subQ1]),TDD([makeQuery(id+"F3.imprint","IMPRINT",EDGE,{"disambiguationData":[TD([[subQ36,-1.0]])],"derivedFrom":subQ1})])]});var subQ39=makeQuery(id+"F4.opExtrude","SWEPT_FACE",FACE,{"disambiguationData":[OSD([subQ1]),TDD([makeQuery(id+"F3.imprint","IMPRINT",EDGE,{"disambiguationData":[TD([[subQ2,1.0]])],"derivedFrom":subQ1})])]});var subQ40=sQuery(id+"F3.wireOp",EDGE,"E7");var subQ41=makeQuery(id+"F4.opExtrude","SWEPT_FACE",FACE,{"disambiguationData":[OSD([subQ40])]});Q0=makeQuery(id+"F6.boolean.opBoolean","SPLIT",FACE,{"disambiguationData":[TD([subQ35,subQ31,subQ16,subQ30,subQ10,makeQuery(id+"F4.boolean.opBoolean","COPY",FACE,{"derivedFrom":subQ37}),makeQuery(id+"F4.boolean.opBoolean","COPY",FACE,{"derivedFrom":subQ33}),makeQuery(id+"F4.boolean.opBoolean","COPY",FACE,{"derivedFrom":subQ20}),makeQuery(id+"F4.boolean.opBoolean","COPY",FACE,{"derivedFrom":subQ39}),makeQuery(id+"F4.boolean.opBoolean","COPY",FACE,{"derivedFrom":subQ41}),makeQuery(id+"F4.boolean.opBoolean","COPY",FACE,{"derivedFrom":subQ29}),makeQuery(id+"F4.boolean.opBoolean","COPY",FACE,{"derivedFrom":subQ26}),makeQuery(id+"F4.boolean.opBoolean","COPY",FACE,{"derivedFrom":subQ24}),makeQuery(id+"F4.boolean.opBoolean","COPY",FACE,{"derivedFrom":subQ23}),makeQuery(id+"F4.boolean.opBoolean","COPY",FACE,{"derivedFrom":subQ22}),makeQuery(id+"F5.boolean.opBoolean","COPY",FACE,{"derivedFrom":makeQuery(id+"F5.opExtrude","SWEPT_FACE",FACE,{"disambiguationData":[OSD([subQ6]),TDD([makeQuery(id+"F3.imprint","IMPRINT",EDGE,{"disambiguationData":[TD([[subQ7,1.0]])],"derivedFrom":subQ6})])]})}),makeQuery(id+"F5.boolean.opBoolean","COPY",FACE,{"derivedFrom":makeQuery(id+"F5.opExtrude","SWEPT_FACE",FACE,{"disambiguationData":[OSD([subQ6]),TDD([makeQuery(id+"F3.imprint","IMPRINT",EDGE,{"disambiguationData":[TD([[subQ11,-1.0]])],"derivedFrom":subQ6})])]})}),makeQuery(id+"F5.boolean.opBoolean","COPY",FACE,{"derivedFrom":makeQuery(id+"F5.opExtrude","SWEPT_FACE",FACE,{"disambiguationData":[OSD([subQ5]),TDD([makeQuery(id+"F3.imprint","IMPRINT",EDGE,{"disambiguationData":[TD([[subQ8,-1.0]])],"derivedFrom":subQ5})])]})}),makeQuery(id+"F6.opExtrude","SWEPT_FACE",FACE,{"disambiguationData":[OSD([subQ6]),TDD([makeQuery(id+"F3.imprint","IMPRINT",EDGE,{"disambiguationData":[TD([[subQ8,1.0]])],"derivedFrom":subQ6})])]}),makeQuery(id+"F6.opExtrude","SWEPT_FACE",FACE,{"disambiguationData":[OSD([subQ5]),TDD([makeQuery(id+"F3.imprint","IMPRINT",EDGE,{"disambiguationData":[TD([[subQ11,1.0]])],"derivedFrom":subQ5})])]}),makeQuery(id+"F6.opExtrude","SWEPT_FACE",FACE,{"disambiguationData":[OSD([subQ5]),TDD([makeQuery(id+"F3.imprint","IMPRINT",EDGE,{"disambiguationData":[TD([[subQ7,-1.0]])],"derivedFrom":subQ5})])]}),makeQuery(id+"F6.opExtrude","SWEPT_FACE",FACE,{"disambiguationData":[OSD([subQ1]),TDD([makeQuery(id+"F3.imprint","IMPRINT",EDGE,{"disambiguationData":[TD([[subQ2,-1.0]])],"derivedFrom":subQ1})])]}),makeQuery(id+"F6.opExtrude","CAP_FACE",FACE,{"disambiguationData":[OSD([subQ1,subQ40,subQ3,subQ34,subQ21,subQ17,subQ0])],"isStart":true}),makeQuery(id+"F6.opExtrude","SWEPT_FACE",FACE,{"disambiguationData":[OSD([subQ1]),TDD([makeQuery(id+"F3.imprint","IMPRINT",EDGE,{"disambiguationData":[TD([[makeQuery(id+"F3.imprint","INTERSECT",VERTEX,{"derivedFrom":[subQ1,subQ34]}),1.0]])],"derivedFrom":subQ1})])]}),makeQuery(id+"F6.opExtrude","SWEPT_FACE",FACE,{"disambiguationData":[OSD([subQ1]),TDD([makeQuery(id+"F3.imprint","IMPRINT",EDGE,{"disambiguationData":[TD([[subQ32,-1.0]])],"derivedFrom":subQ1})])]}),makeQuery(id+"F6.opExtrude","SWEPT_FACE",FACE,{"disambiguationData":[OSD([subQ1]),TDD([makeQuery(id+"F3.imprint","IMPRINT",EDGE,{"disambiguationData":[TD([[subQ19,-1.0]])],"derivedFrom":subQ1})])]}),makeQuery(id+"F6.opExtrude","SWEPT_FACE",FACE,{"disambiguationData":[OSD([subQ40])]}),makeQuery(id+"F6.opExtrude","SWEPT_FACE",FACE,{"disambiguationData":[OSD([subQ3]),TDD([makeQuery(id+"F3.imprint","IMPRINT",EDGE,{"disambiguationData":[TD([[subQ36,1.0]])],"derivedFrom":subQ3})])]}),makeQuery(id+"F6.opExtrude","SWEPT_FACE",FACE,{"disambiguationData":[OSD([subQ34])]}),makeQuery(id+"F6.opExtrude","SWEPT_FACE",FACE,{"disambiguationData":[OSD([subQ21])]}),makeQuery(id+"F6.opExtrude","SWEPT_FACE",FACE,{"disambiguationData":[OSD([subQ17])]}),makeQuery(id+"F6.opExtrude","SWEPT_FACE",FACE,{"disambiguationData":[OSD([subQ0])]})])],"derivedFrom":makeQuery(id+"F4.boolean.opBoolean","SPLIT",FACE,{"disambiguationData":[TD([subQ30])],"derivedFrom":subQ35})});}
            var sketch = newSketch(context, id + "F18", { "sketchPlane" : qUnion([Q0])});
            skText(sketch, "E44", { "text": "NICHOLSON\n  BREWING", "fontName": "NotoSerif-Bold.ttf"});
            const initialGuessF18  = {"E44": [-0.0145, 0.11805, 1, 0, 0.00343]};
            skSetInitialGuess(sketch, initialGuessF18);
            skSolve(sketch);
        }
        {
            var Q0;
            Q0 = qSketchRegion(id + "F17", true);
            extrude(context, id + "F19", {"entities" : qUnion([Q0]), "operationType" : NewBodyOperationType.ADD, "oppositeDirection" : true, "depth" : 6.35 * mm, "offsetDistance" : 25.4 * mm});
        }
        {
            var Q0;
            Q0 = qSketchRegion(id + "F18", true);
            extrude(context, id + "F20", {"entities" : qUnion([Q0]), "operationType" : NewBodyOperationType.ADD, "depth" : 1.9 * mm, "offsetDistance" : 25.4 * mm});
        }
        {
            var Q0;
            Q0=makeQuery(id+"F8.opExtrude","CAP_EDGE",EDGE,{"disambiguationData":[OSD([sQuery(id+"F2.wireOp",EDGE,"E1")])],"isStart":false});
            var Q1;
            Q1=makeQuery(id+"F1.opExtrude","SWEPT_EDGE",EDGE,{"disambiguationData":[OSD([sQuery(id+"F0.wireOp",EDGE,"E0.bottom"),sQuery(id+"F0.wireOp",EDGE,"E0.left")])]});
            var Q2;
            Q2=makeQuery(id+"F1.opExtrude","SWEPT_EDGE",EDGE,{"disambiguationData":[OSD([sQuery(id+"F0.wireOp",EDGE,"E0.bottom"),sQuery(id+"F0.wireOp",EDGE,"E0.right")])]});
            var Q3;
            Q3=makeQuery(id+"F1.opExtrude","SWEPT_EDGE",EDGE,{"disambiguationData":[OSD([sQuery(id+"F0.wireOp",EDGE,"E0.top"),sQuery(id+"F0.wireOp",EDGE,"E0.left")])]});
            var Q4;
            Q4=makeQuery(id+"F8.opExtrude","CAP_EDGE",EDGE,{"disambiguationData":[OSD([sQuery(id+"F2.wireOp",EDGE,"E1")])],"isStart":true});
            var Q5;
            Q5=makeQuery(id+"F1.opExtrude","SWEPT_EDGE",EDGE,{"disambiguationData":[OSD([sQuery(id+"F0.wireOp",EDGE,"E0.top"),sQuery(id+"F0.wireOp",EDGE,"E0.right")])]});
            fillet(context, id + "F21", {"entities" : qUnion([Q0, Q1, Q2, Q3, Q4, Q5]), "radius" : 3.17 * mm, "tangentPropagation" : true, "allowEdgeOverflow" : false});
        }
        {
            var Q0;
            Q0=makeQuery(id+"F1.opExtrude","CAP_FACE",FACE,{"disambiguationData":[OSD([sQuery(id+"F0.wireOp",EDGE,"E0.bottom"),sQuery(id+"F0.wireOp",EDGE,"E0.top"),sQuery(id+"F0.wireOp",EDGE,"E0.left"),sQuery(id+"F0.wireOp",EDGE,"E0.right")])],"isStart":true});
            var sketch = newSketch(context, id + "F22", { "sketchPlane" : qUnion([Q0])});
            skCircle(sketch, "E45", {"center": v(0, 0) * mm, "radius": 6.35 * mm});
            skSolve(sketch);
        }
        {
            var Q0;
            Q0=makeQuery(id+"F22.imprint","IMPRINT",FACE,{"disambiguationData":[TD([[makeQuery(id+"F22.imprint","IMPRINT",EDGE,{"derivedFrom":sQuery(id+"F22.wireOp",EDGE,"E45")}),1.0]])]});
            extrude(context, id + "F23", {"entities" : qUnion([Q0]), "operationType" : NewBodyOperationType.REMOVE, "oppositeDirection" : true, "depth" : 19.05 * mm, "offsetDistance" : 25.4 * mm});
        }
    });
